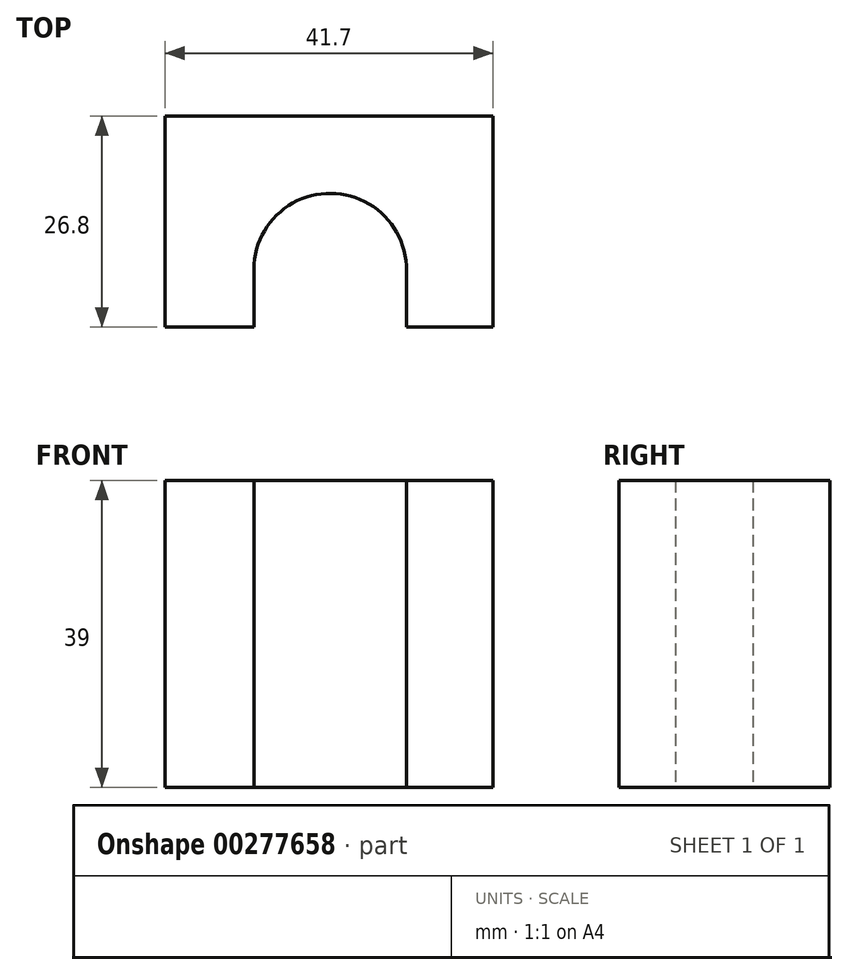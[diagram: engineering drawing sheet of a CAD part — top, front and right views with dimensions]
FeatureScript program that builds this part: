
annotation { "Feature Type Name" : "Feature", "Feature Type Description" : "" }
export const myFeature = defineFeature(function(context is Context, id is Id, definition is map)
    precondition{}
    {
        {
            var Q0;
            Q0=qCreatedBy(makeId("Top.planeOp"),FACE);
            var sketch = newSketch(context, id + "F0", { "sketchPlane" : qUnion([Q0])});
            skLineSegment(sketch, "E0.bottom", {"start": v(0, 0) * mm, "end": v(11.31, 0) * mm});
            skLineSegment(sketch, "E0.top", {"start": v(0, 26.8) * mm, "end": v(41.7, 26.8) * mm});
            skLineSegment(sketch, "E0.left", {"start": v(0, 0) * mm, "end": v(0, 26.8) * mm});
            skLineSegment(sketch, "E0.right", {"start": v(41.7, 0) * mm, "end": v(41.7, 26.8) * mm});
            skArc(sketch, "E1", {"start": v(30.7, 7.17) * mm, "mid": v(21.1, 16.98) * mm, "end": v(11.31, 7.38) * mm});
            skLineSegment(sketch, "E2.trimOffspring", {"start": v(30.7, 0) * mm, "end": v(41.7, 0) * mm});
            skLineSegment(sketch, "E3", {"start": v(11.31, 7.38) * mm, "end": v(11.31, 0) * mm});
            skLineSegment(sketch, "E4", {"start": v(30.7, 7.17) * mm, "end": v(30.7, 0) * mm});
            skSolve(sketch);
        }
        {
            var Q0;
            Q0=makeQuery(id+"F0.imprint","IMPRINT",FACE,{"disambiguationData":[TD([[makeQuery(id+"F0.imprint","IMPRINT",EDGE,{"derivedFrom":sQuery(id+"F0.wireOp",EDGE,"E0.bottom")}),1.0]])]});
            extrude(context, id + "F1", {"entities" : qUnion([Q0]), "depth" : 39 * mm});
        }
    });
